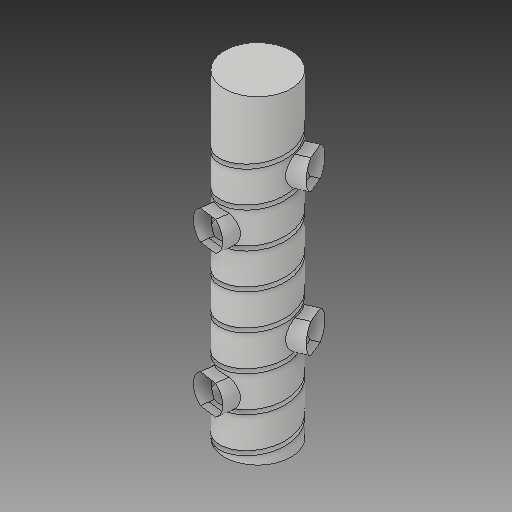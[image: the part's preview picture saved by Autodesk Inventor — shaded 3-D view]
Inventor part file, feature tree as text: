
AUTODESK INVENTOR PART (.ipt)
format: ipt  version: 2017 (Build 210142000, 142)  size: 930,816 bytes
history: native  units: in
note: dims shown in document units (in); Inventor stores cm internally (conversion verified against a paired STEP export)
features: extrude x25, other x15, sketch x14, loft x6, shell x1, plane x1, delete_face x1
ambient origin geometry x8: Origin, YZ Plane, XZ Plane, XY Plane, X Axis, Y Axis, Z Axis, Center Point
bodies: Body1 (feature_tree), Body2 (feature_tree)
feature tree (63):
  shell  "shell and ramp"  Thickness=15.0in
  extrude  "outer cassing"  Depth=72.0in TaperAngle=0.0deg
  extrude  "bottom"  Depth=3.5in
  other  "Work Axis1"
  other  "ramp"
  other  "top floor fill workplane"
  extrude  "top floor fill"  Depth=0.5in
  sketch  "Sketch5"  dims[d53=3.0in d54=0.5in]
  other  "railing complete"
  other  "light ramp to complete"
  extrude  "top cap"  Depth=9.0in
  plane  "workplane sketch"
  other  "connection plane 1"
  other  "connection plane 2"
  other  "connection workplane 3"
  extrude  "bottom connection"  TaperAngle=90.0deg  [1 undecoded]
  extrude  "bottom connect to case"  TaperAngle=90.0deg  [1 undecoded]
  extrude  "connection cut"  Depth=1.0in TaperAngle=0.0deg
  sketch  "Sketch20"  dims[d55=3.0in]
  extrude  "connetion 2"  Depth=9.48in
  extrude  "connection to case 2"  Depth=1.0in TaperAngle=0.0deg
  extrude  "connection cut 2"  Depth=6.6667in TaperAngle=0.0deg
  loft  "connection ramp 2"
  extrude  "connection 3"  Depth=30.81in
  extrude  "connection to case 3"  Depth=1.0in TaperAngle=0.0deg
  extrude  "connection cut 3"  Depth=1.0in TaperAngle=0.0deg
  loft  "connetion ramp 3"
  sketch  "Sketch23"  dims[d64=8.0in d65=1.0in d66=3.1201in d67=0.0in d68=90.0deg d69=90.0deg d70=0.0in d71=0.0in d146=9.0in]
  extrude  "connection 4"  Depth=6.6667in TaperAngle=0.0deg
  extrude  "connection to case 4"  Depth=1.0in TaperAngle=0.0deg
  extrude  "connection cut 4"  Depth=1.0in TaperAngle=0.0deg
  loft  "connection ramp 4"
  sketch  "Sketch24"  dims[d147=1.1811in d149=360.0deg d151=90.0deg]
  extrude  "connection 5"  Depth=6.6667in TaperAngle=0.0deg
  extrude  "connection to case 5"  Depth=1.0in TaperAngle=0.0deg
  extrude  "connection cut 5"  Depth=1.0in TaperAngle=0.0deg
  loft  "connection ramp 5"
  sketch  "Sketch25"  dims[d152=90.0deg d153=90.0deg]
  extrude  "connection 6"  Depth=62.8in
  extrude  "connection to case 6"  Depth=1.0in TaperAngle=0.0deg
  extrude  "connection cut 6"  Depth=1.0in TaperAngle=0.0deg
  loft  "connection ramp 6"
  sketch  "Sketch26"  dims[d154=6.6667in d157=4.8944in d158=1.0in d159=0.0in d160=1.0in d161=0.0in]
  extrude  "connection 7"  Depth=1.0in TaperAngle=0.0deg
  extrude  "connection to case 7"  Depth=1.0in TaperAngle=0.0deg
  extrude  "connection cut 7"  Depth=1.0in TaperAngle=0.0deg
  loft  "connection ramp 7"
  delete_face  "Delete Face1"
  sketch  "Sketch1"  dims[d1=16.0in d2=72.0in d3=0.0in]
  sketch  "Sketch4"  dims[d40=1.0in d41=0.0in d44=3.5in]
  sketch  "Sketch27"  dims[d162=2.6875in d163=0.0in d164=9.48in]
  sketch  "Sketch28"  dims[d165=6.6667in d168=4.8944in d169=1.0in d170=0.0in d171=1.0in d172=0.0in]
  other  "light railing complete"
  sketch  "Sketch29"  dims[d173=2.625in d174=0.0in d178=6.6667in d181=4.8944in d182=1.0in d183=0.0in]
  sketch  "Sketch30"  dims[d184=1.0in d185=0.0in d186=1.0in d187=0.0in]
  other  "Edges2"
  sketch  "Sketch32"  dims[d188=20.15in d189=30.81in]
  other  "Edges4"
  sketch  "Sketch33"  dims[d190=6.6667in d193=4.8944in d194=1.0in d195=0.0in d196=1.0in d197=0.0in d198=1.0in d199=0.0in d200=41.48in d201=6.6667in d204=4.8944in d205=1.0in d206=0.0in d207=1.0in d208=0.0in d209=1.0in d210=0.0in d211=52.15in d213=6.6667in d216=4.8944in d217=1.0in d218=0.0in d219=1.0in d220=0.0in d221=1.0in d222=0.0in d228=6.6667in d231=4.8944in d232=62.8in d233=1.0in d234=0.0in d237=1.0in d238=0.0in d239=0.0in d240=1.0in d241=0.0in d242=1.0in d243=0.0in d244=1.0in d245=0.0in d308=3.0in d309=0.5in d310=3.0in d321=90.0deg d322=90.0deg d323=0.0in d324=90.0deg d325=0.0in d326=90.0deg d327=1.0in d329=1.0in d330=0.0in d331=90.0deg d332=0.0in d333=90.0deg d335=1.0in d336=0.0in d337=90.0deg d338=0.0in d339=90.0deg d340=1.0in d341=0.0in d342=90.0deg d343=0.0in d344=90.0deg d346=1.0in d347=0.0in d348=90.0deg d349=0.0in d350=90.0deg d353=1.0in d354=0.0in d355=90.0deg d356=0.0in d357=90.0deg d448=4.0in d450=3.8873in d451=3.8873in d455=1.6458in d460=3.3333in d462=1.0in d477=4.0in d479=3.8873in d480=3.8873in d484=1.6458in d489=3.3333in d491=1.0in d492=4.0in d494=3.8873in d495=3.8873in d499=1.6458in d504=3.3333in d506=1.0in d507=4.0in d509=3.8873in d510=3.8873in d514=1.6458in d519=3.3333in d521=1.0in d522=4.0in d524=3.8873in d525=3.8873in d529=1.6458in d534=3.3333in d536=1.0in d537=4.0in d539=3.8873in d540=3.8873in d544=1.6458in d549=3.3333in d551=1.0in d552=4.0in d554=3.8873in d555=3.8873in d559=1.6458in d564=3.3333in d566=1.0in]
  other  "Edges5"
  other  "Edges6"
  other  "Edges1"
  other  "Edges3"
note: 2 required parameter values undecoded (feature->parameter linkage not recoverable at this tier; creation-order binding heuristic only, values carry confidence <= 0.55)
